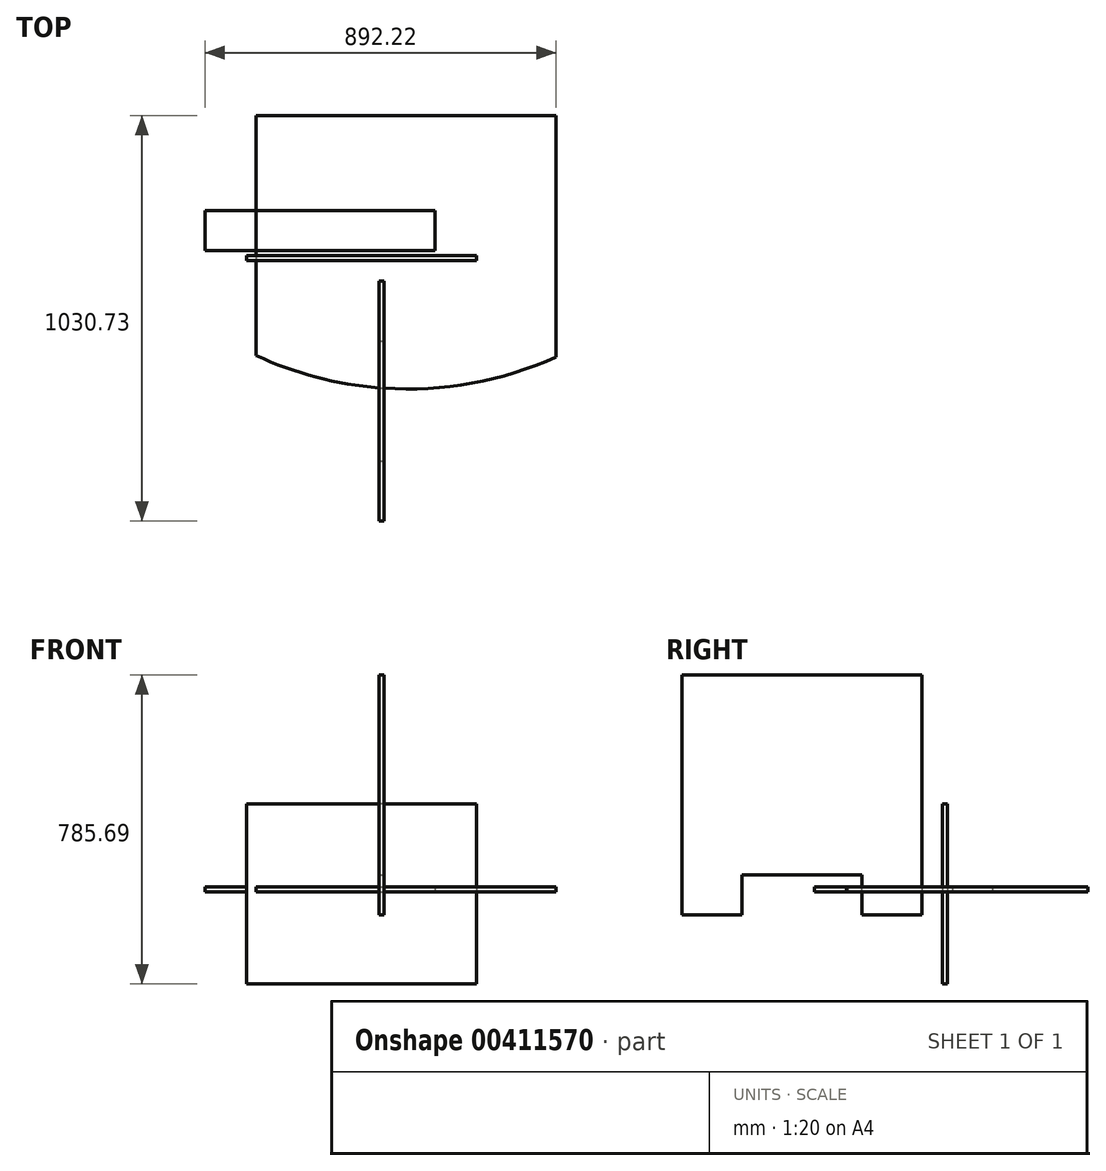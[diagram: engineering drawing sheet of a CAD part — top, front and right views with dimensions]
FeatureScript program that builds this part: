
annotation { "Feature Type Name" : "Feature", "Feature Type Description" : "" }
export const myFeature = defineFeature(function(context is Context, id is Id, definition is map)
    precondition{}
    {
        {
            var Q0;
            Q0=qCreatedBy(makeId("Top.planeOp"),FACE);
            var sketch = newSketch(context, id + "F0", { "sketchPlane" : qUnion([Q0])});
            skLineSegment(sketch, "E0.bottom", {"start": v(-324.96, 355.96) * mm, "end": v(437.04, 355.96) * mm});
            skLineSegment(sketch, "E0.left", {"start": v(-324.96, 355.96) * mm, "end": v(-324.96, -253.64) * mm});
            skLineSegment(sketch, "E0.right", {"start": v(437.04, 355.96) * mm, "end": v(437.04, -257.6) * mm});
            skArc(sketch, "E1", {"start": v(-324.96, -253.64) * mm, "mid": v(55.6, -338.77) * mm, "end": v(437.04, -257.6) * mm});
            skSolve(sketch);
        }
        {
            var Q0;
            Q0=makeQuery(id+"F0.imprint","IMPRINT",FACE,{"disambiguationData":[TD([[makeQuery(id+"F0.imprint","IMPRINT",EDGE,{"derivedFrom":sQuery(id+"F0.wireOp",EDGE,"E0.bottom")}),-1.0]])]});
            extrude(context, id + "F1", {"entities" : qUnion([Q0]), "depth" : 12.7 * mm});
        }
        {
            var Q0;
            Q0=qCreatedBy(makeId("Right.planeOp"),FACE);
            var sketch = newSketch(context, id + "F2", { "sketchPlane" : qUnion([Q0])});
            skLineSegment(sketch, "E2.bottom", {"start": v(-674.77, 551.16) * mm, "end": v(-65.17, 551.16) * mm});
            skLineSegment(sketch, "E2.left", {"start": v(-674.77, 551.16) * mm, "end": v(-674.77, -58.44) * mm});
            skLineSegment(sketch, "E2.right", {"start": v(-65.17, 551.16) * mm, "end": v(-65.17, -58.44) * mm});
            skLineSegment(sketch, "E3.top", {"start": v(-522.37, 43.16) * mm, "end": v(-217.57, 43.16) * mm});
            skLineSegment(sketch, "E3.left", {"start": v(-522.37, -58.44) * mm, "end": v(-522.37, 43.16) * mm});
            skLineSegment(sketch, "E3.right", {"start": v(-217.57, -58.44) * mm, "end": v(-217.57, 43.16) * mm});
            skPoint(sketch, "E4", {"position": v(-522.37, -58.44) * mm});
            skPoint(sketch, "E5", {"position": v(-217.57, -58.44) * mm});
            skLineSegment(sketch, "E6", {"start": v(-674.77, -58.44) * mm, "end": v(-522.37, -58.44) * mm});
            skLineSegment(sketch, "E7", {"start": v(-217.57, -58.44) * mm, "end": v(-65.17, -58.44) * mm});
            skPoint(sketch, "E8", {"position": v(-674.77, 335.26) * mm});
            skPoint(sketch, "E9", {"position": v(-674.77, 106.66) * mm});
            skSolve(sketch);
        }
        {
            var Q0;
            Q0=makeQuery(id+"F2.imprint","IMPRINT",FACE,{"disambiguationData":[TD([[makeQuery(id+"F2.imprint","IMPRINT",EDGE,{"derivedFrom":sQuery(id+"F2.wireOp",EDGE,"E2.bottom")}),-1.0]])]});
            extrude(context, id + "F3", {"entities" : qUnion([Q0]), "oppositeDirection" : true, "depth" : 12.7 * mm});
        }
        {
            var Q0;
            Q0=qCreatedBy(makeId("Front.planeOp"),FACE);
            var sketch = newSketch(context, id + "F4", { "sketchPlane" : qUnion([Q0])});
            skLineSegment(sketch, "E10.bottom", {"start": v(234.6, 222.67) * mm, "end": v(-349.6, 222.67) * mm});
            skLineSegment(sketch, "E10.top", {"start": v(234.6, -234.53) * mm, "end": v(-349.6, -234.53) * mm});
            skLineSegment(sketch, "E10.left", {"start": v(234.6, 222.67) * mm, "end": v(234.6, -234.53) * mm});
            skLineSegment(sketch, "E10.right", {"start": v(-349.6, 222.67) * mm, "end": v(-349.6, -234.53) * mm});
            skSolve(sketch);
        }
        {
            var Q0;
            Q0=makeQuery(id+"F4.imprint","IMPRINT",FACE,{"disambiguationData":[TD([[makeQuery(id+"F4.imprint","IMPRINT",EDGE,{"derivedFrom":sQuery(id+"F4.wireOp",EDGE,"E10.bottom")}),1.0]])]});
            extrude(context, id + "F5", {"entities" : qUnion([Q0]), "depth" : 12.7 * mm});
        }
        {
            var Q0;
            Q0=qCreatedBy(makeId("Top.planeOp"),FACE);
            var sketch = newSketch(context, id + "F6", { "sketchPlane" : qUnion([Q0])});
            skLineSegment(sketch, "E11.bottom", {"start": v(-455.18, 113.98) * mm, "end": v(129.02, 113.98) * mm});
            skLineSegment(sketch, "E11.top", {"start": v(-455.18, 12.38) * mm, "end": v(129.02, 12.38) * mm});
            skLineSegment(sketch, "E11.left", {"start": v(-455.18, 113.98) * mm, "end": v(-455.18, 12.38) * mm});
            skLineSegment(sketch, "E11.right", {"start": v(129.02, 113.98) * mm, "end": v(129.02, 12.38) * mm});
            skSolve(sketch);
        }
        {
            var Q0;
            Q0=makeQuery(id+"F6.imprint","IMPRINT",FACE,{"disambiguationData":[TD([[makeQuery(id+"F6.imprint","IMPRINT",EDGE,{"derivedFrom":sQuery(id+"F6.wireOp",EDGE,"E11.bottom")}),-1.0]])]});
            extrude(context, id + "F7", {"entities" : qUnion([Q0]), "depth" : 12.7 * mm});
        }
    });
